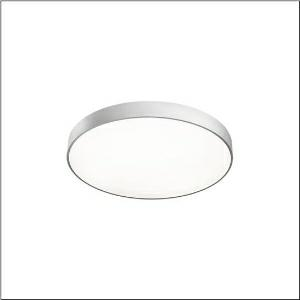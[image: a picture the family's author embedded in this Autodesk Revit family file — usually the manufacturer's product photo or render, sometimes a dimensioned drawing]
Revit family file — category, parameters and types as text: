
# Revit family: round_21_m_51mr36fd0321s
name_source: partatom
category: Lighting Fixtures
units: mm (PartAtom-declared; Revit-internal decimal feet)

## family parameters
Cut with Voids When Loaded = No
Host = Face
Light Source = No
Part Type = Normal
Room Calculation Point = No
Round Connector Dimension = Use Diameter
Shared = No

## types (1)
- Round 21 M (1 x LED, 7500 lm, 54.9 W, 3000K)
    Apparent Load = 55 VA
    CIE Flux Codes = 49 80 96 100 100
    Color Rendering = 80
    Color Temperature = 3000K
    Default Elevation = 1800 mm
    Description = Round 21 M, wall and ceiling luminaire, primary optical cover: cover, of PMMA, opal, light emission: direct distribution, primary light characteristic: symmetric, installation type: suspended mounting, surface-mounted, LED, rated luminous flux: 7.500lm, luminous efficacy: 137lm/W, light colour: 830, colour temperature: 3000K, control gear: DALI 2, with terminal, 5-pole, mains connection: 230V, AC, 50/60Hz, rated input power: 54.8W, housing, of aluminium, coated, silver, diameter: 600mm, height: 62mm, protection rating (complete): IP40, insulation class (complete): insulation class I (protective earthing), certification: CE, impact resistance: IK04, permissible operating ambient temperature: -10..+35°C, packaging unit: 1 piece
    Height = 87 mm
    Lamp = 1 x LED
    Lamp Light Flux = 7500 lm
    Lamp Power = 54.9 W
    Lamp count = 1
    Length = 600 mm
    Luminous efficacy = 137 lm/W
    Manufacturer = Siteco
    ModVariant = No
    Model = 51MR36FD0321S
    Mounting Place = Ceiling
    Mounting Type = Surface mounted
    Number of Poles = 1
    OnlyDefault = Yes
    Power Factor = 1
    Product Name = Round 21 M
    Product group = wall and ceiling luminaire
    ProductGroupID = 304
    Protection Class = Protection class I
    Protection Degree = IP 40
    RLX_Detail_Level = 1
    RLX_Emergency_Light_Flux = 0 lm
    RLX_Emergency_Type = 0
    RLX_Emergency_Type_DB = No
    RlxData = <blob elided: 14829 chars, md5=6b96d760>
    Socket = socket
    Standby Power = 0 W
    System Light Flux = 7500 lm
    System Power = 55 W
    Type Comments = Product without accessories
    Type Image = l_1258303.jpg
    URL = http://relux.com
    VarID = ---
    Voltage = 0 V
    Weight = 0.00 kg
    Width = 0 mm  [stored 0 ft]

note: [stored X ft] marks values corroborated as IEEE doubles in the binary element streams (Revit-internal decimal feet)

## geometry (parser evidence)
native form markers: Sweep x12
no freeform markers — native parametric forms only
